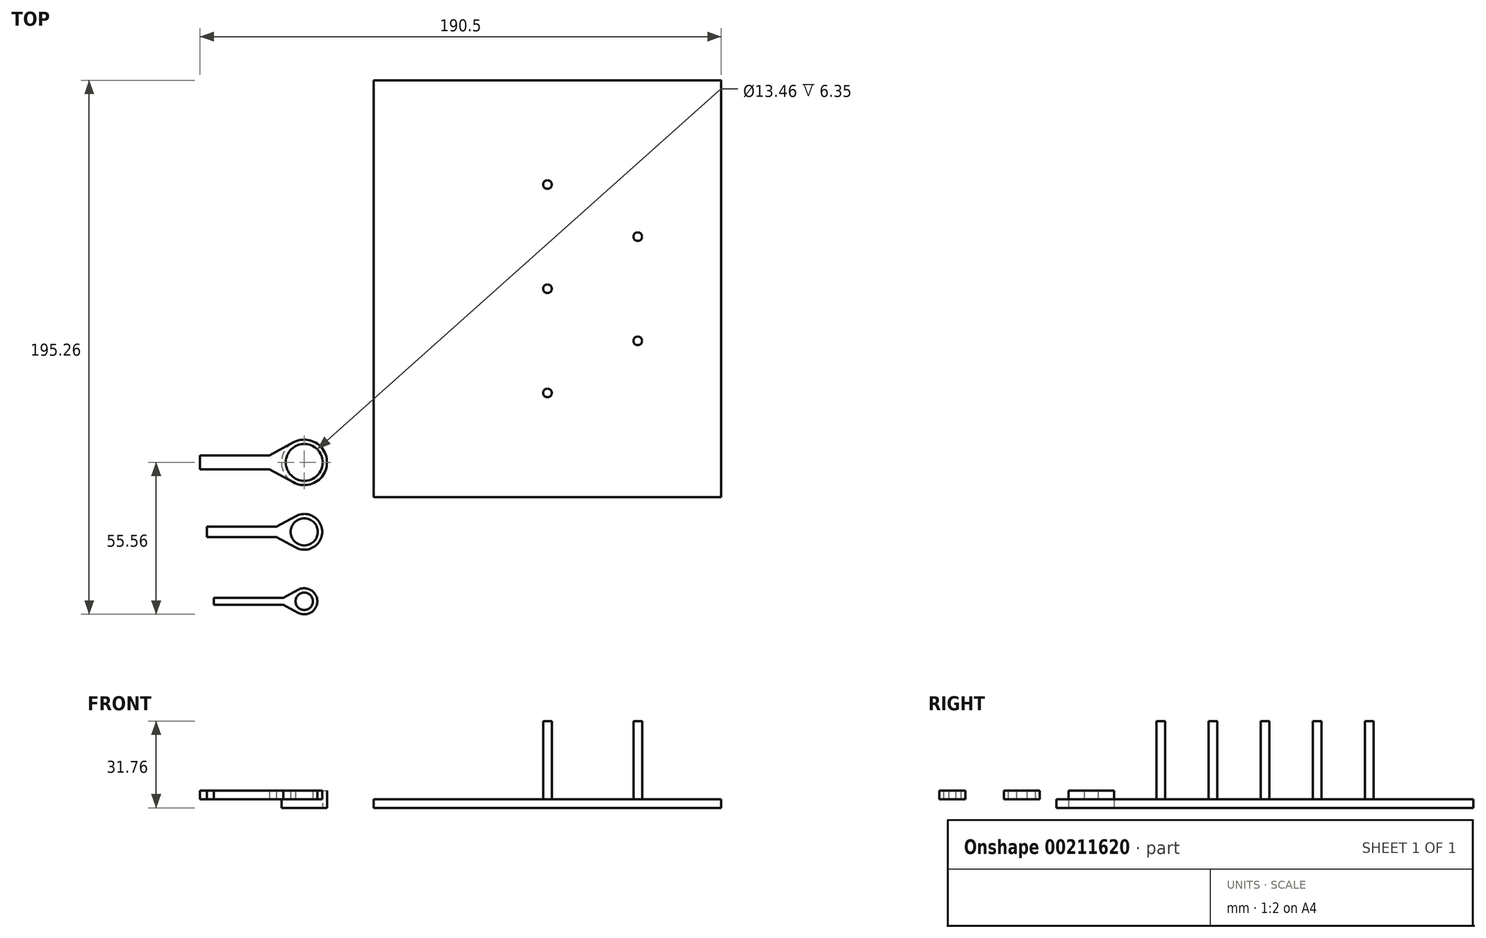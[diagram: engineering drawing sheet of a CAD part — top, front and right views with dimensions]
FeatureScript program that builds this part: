
annotation { "Feature Type Name" : "Feature", "Feature Type Description" : "" }
export const myFeature = defineFeature(function(context is Context, id is Id, definition is map)
    precondition{}
    {
        {
            var Q0;
            Q0=qCreatedBy(makeId("Top.planeOp"),FACE);
            var sketch = newSketch(context, id + "F0", { "sketchPlane" : qUnion([Q0])});
            skLineSegment(sketch, "E0.bottom", {"start": v(0, 152.4) * mm, "end": v(127, 152.4) * mm});
            skLineSegment(sketch, "E0.top", {"start": v(0, 0) * mm, "end": v(127, 0) * mm});
            skLineSegment(sketch, "E0.left", {"start": v(0, 152.4) * mm, "end": v(0, 0) * mm});
            skLineSegment(sketch, "E0.right", {"start": v(127, 152.4) * mm, "end": v(127, 0) * mm});
            skCircle(sketch, "E1", {"center": v(63.5, 76.2) * mm, "radius": 1.59 * mm});
            skCircle(sketch, "E2", {"center": v(63.5, 38.1) * mm, "radius": 1.59 * mm});
            skCircle(sketch, "E3.1.0", {"center": v(96.5, 57.15) * mm, "radius": 1.59 * mm});
            skCircle(sketch, "E3.2.0", {"center": v(96.5, 95.25) * mm, "radius": 1.59 * mm});
            skCircle(sketch, "E3.3.0", {"center": v(63.5, 114.3) * mm, "radius": 1.59 * mm});
            skCircle(sketch, "E3.4.0", {"center": v(30.5, 95.25) * mm, "radius": 1.59 * mm});
            skCircle(sketch, "E3.5.0", {"center": v(30.5, 57.15) * mm, "radius": 1.59 * mm});
            skCircle(sketch, "E4", {"center": v(-25.4, 12.7) * mm, "radius": 8.32 * mm});
            skLineSegment(sketch, "E5.bottom", {"start": v(-63.5, 15.24) * mm, "end": v(-38.1, 15.24) * mm});
            skLineSegment(sketch, "E5.top", {"start": v(-63.5, 10.16) * mm, "end": v(-38.1, 10.16) * mm});
            skLineSegment(sketch, "E5.left", {"start": v(-63.5, 15.24) * mm, "end": v(-63.5, 10.16) * mm});
            skLineSegment(sketch, "E5.right", {"start": v(-38.1, 15.24) * mm, "end": v(-38.1, 10.16) * mm});
            skLineSegment(sketch, "E6", {"start": v(-38.1, 15.24) * mm, "end": v(-29.39, 20) * mm});
            skLineSegment(sketch, "E7", {"start": v(-38.1, 10.16) * mm, "end": v(-29.39, 5.4) * mm});
            skLineSegment(sketch, "E8", {"start": v(-25.4, 12.7) * mm, "end": v(-38.1, 12.7) * mm});
            skCircle(sketch, "E9", {"center": v(-25.4, 12.7) * mm, "radius": 6.73 * mm});
            skCircle(sketch, "E10", {"center": v(-25.4, -12.7) * mm, "radius": 6.54 * mm});
            skLineSegment(sketch, "E11.bottom", {"start": v(-60.96, -10.8) * mm, "end": v(-35.56, -10.8) * mm});
            skLineSegment(sketch, "E11.top", {"start": v(-60.96, -14.6) * mm, "end": v(-35.56, -14.6) * mm});
            skLineSegment(sketch, "E11.left", {"start": v(-60.96, -10.8) * mm, "end": v(-60.96, -14.6) * mm});
            skLineSegment(sketch, "E11.right", {"start": v(-35.56, -10.8) * mm, "end": v(-35.56, -14.6) * mm});
            skLineSegment(sketch, "E12", {"start": v(-35.56, -10.8) * mm, "end": v(-28.53, -6.96) * mm});
            skLineSegment(sketch, "E13", {"start": v(-35.56, -14.6) * mm, "end": v(-28.53, -18.44) * mm});
            skLineSegment(sketch, "E14", {"start": v(-25.4, -12.7) * mm, "end": v(-35.56, -12.7) * mm});
            skCircle(sketch, "E15", {"center": v(-25.4, -12.7) * mm, "radius": 4.95 * mm});
            skCircle(sketch, "E16", {"center": v(-25.4, -38.1) * mm, "radius": 4.76 * mm});
            skLineSegment(sketch, "E17.bottom", {"start": v(-58.42, -36.83) * mm, "end": v(-33.02, -36.83) * mm});
            skLineSegment(sketch, "E17.top", {"start": v(-58.42, -39.37) * mm, "end": v(-33.02, -39.37) * mm});
            skLineSegment(sketch, "E17.left", {"start": v(-58.42, -36.83) * mm, "end": v(-58.42, -39.37) * mm});
            skLineSegment(sketch, "E17.right", {"start": v(-33.02, -36.83) * mm, "end": v(-33.02, -39.37) * mm});
            skLineSegment(sketch, "E18", {"start": v(-33.02, -36.83) * mm, "end": v(-27.68, -33.92) * mm});
            skLineSegment(sketch, "E19", {"start": v(-33.02, -39.37) * mm, "end": v(-27.68, -42.28) * mm});
            skLineSegment(sketch, "E20", {"start": v(-25.4, -38.1) * mm, "end": v(-33.02, -38.1) * mm});
            skCircle(sketch, "E21", {"center": v(-25.4, -38.1) * mm, "radius": 3.18 * mm});
            skSolve(sketch);
        }
        {
            var Q0;
            Q0=makeQuery(id+"F0.imprint","IMPRINT",FACE,{"disambiguationData":[TD([[makeQuery(id+"F0.imprint","IMPRINT",EDGE,{"derivedFrom":sQuery(id+"F0.wireOp",EDGE,"E0.bottom")}),-1.0]])]});
            var Q1;
            Q1=makeQuery(id+"F0.imprint","IMPRINT",FACE,{"disambiguationData":[TD([[makeQuery(id+"F0.imprint","IMPRINT",EDGE,{"derivedFrom":sQuery(id+"F0.wireOp",EDGE,"E3.3.0")}),1.0]])]});
            var Q2;
            Q2=makeQuery(id+"F0.imprint","IMPRINT",FACE,{"disambiguationData":[TD([[makeQuery(id+"F0.imprint","IMPRINT",EDGE,{"derivedFrom":sQuery(id+"F0.wireOp",EDGE,"E3.2.0")}),1.0]])]});
            var Q3;
            Q3=makeQuery(id+"F0.imprint","IMPRINT",FACE,{"disambiguationData":[TD([[makeQuery(id+"F0.imprint","IMPRINT",EDGE,{"derivedFrom":sQuery(id+"F0.wireOp",EDGE,"E3.1.0")}),1.0]])]});
            var Q4;
            Q4=makeQuery(id+"F0.imprint","IMPRINT",FACE,{"disambiguationData":[TD([[makeQuery(id+"F0.imprint","IMPRINT",EDGE,{"derivedFrom":sQuery(id+"F0.wireOp",EDGE,"E2")}),1.0]])]});
            var Q5;
            Q5=makeQuery(id+"F0.imprint","IMPRINT",FACE,{"disambiguationData":[TD([[makeQuery(id+"F0.imprint","IMPRINT",EDGE,{"derivedFrom":sQuery(id+"F0.wireOp",EDGE,"E3.5.0")}),1.0]])]});
            var Q6;
            Q6=makeQuery(id+"F0.imprint","IMPRINT",FACE,{"disambiguationData":[TD([[makeQuery(id+"F0.imprint","IMPRINT",EDGE,{"derivedFrom":sQuery(id+"F0.wireOp",EDGE,"E3.4.0")}),1.0]])]});
            var Q7;
            Q7=makeQuery(id+"F0.imprint","IMPRINT",FACE,{"disambiguationData":[TD([[makeQuery(id+"F0.imprint","IMPRINT",EDGE,{"derivedFrom":sQuery(id+"F0.wireOp",EDGE,"E1")}),1.0]])]});
            extrude(context, id + "F1", {"entities" : qUnion([Q0, Q1, Q2, Q3, Q4, Q5, Q6, Q7]), "oppositeDirection" : true, "depth" : 3.17 * mm});
        }
        {
            var Q0;
            Q0=makeQuery(id+"F0.imprint","IMPRINT",FACE,{"disambiguationData":[TD([[makeQuery(id+"F0.imprint","IMPRINT",EDGE,{"derivedFrom":sQuery(id+"F0.wireOp",EDGE,"E3.3.0")}),1.0]])]});
            var Q1;
            Q1=makeQuery(id+"F0.imprint","IMPRINT",FACE,{"disambiguationData":[TD([[makeQuery(id+"F0.imprint","IMPRINT",EDGE,{"derivedFrom":sQuery(id+"F0.wireOp",EDGE,"E3.2.0")}),1.0]])]});
            var Q2;
            Q2=makeQuery(id+"F0.imprint","IMPRINT",FACE,{"disambiguationData":[TD([[makeQuery(id+"F0.imprint","IMPRINT",EDGE,{"derivedFrom":sQuery(id+"F0.wireOp",EDGE,"E1")}),1.0]])]});
            var Q3;
            Q3=makeQuery(id+"F0.imprint","IMPRINT",FACE,{"disambiguationData":[TD([[makeQuery(id+"F0.imprint","IMPRINT",EDGE,{"derivedFrom":sQuery(id+"F0.wireOp",EDGE,"E3.1.0")}),1.0]])]});
            var Q4;
            Q4=makeQuery(id+"F0.imprint","IMPRINT",FACE,{"disambiguationData":[TD([[makeQuery(id+"F0.imprint","IMPRINT",EDGE,{"derivedFrom":sQuery(id+"F0.wireOp",EDGE,"E2")}),1.0]])]});
            var Q5;
            Q5=sQuery(id+"F0.wireOp",EDGE,"E3.3.0");
            var Q6;
            Q6=sQuery(id+"F0.wireOp",EDGE,"E3.2.0");
            var Q7;
            Q7=sQuery(id+"F0.wireOp",EDGE,"E3.1.0");
            var Q8;
            Q8=sQuery(id+"F0.wireOp",EDGE,"E2");
            var Q9;
            Q9=sQuery(id+"F0.wireOp",EDGE,"E3.5.0");
            var Q10;
            Q10=sQuery(id+"F0.wireOp",EDGE,"E3.4.0");
            var Q11;
            Q11=sQuery(id+"F0.wireOp",EDGE,"E1");
            extrude(context, id + "F2", {"entities" : qUnion([Q0, Q1, Q2, Q3, Q4]), "operationType" : NewBodyOperationType.ADD, "surfaceEntities" : qUnion([Q5, Q6, Q7, Q8, Q9, Q10, Q11]), "depth" : 28.57 * mm});
        }
        {
            var Q0;
            Q0=makeQuery(id+"F0.imprint","IMPRINT",FACE,{"disambiguationData":[TD([[makeQuery(id+"F0.imprint","IMPRINT",EDGE,{"derivedFrom":sQuery(id+"F0.wireOp",EDGE,"E9")}),-1.0]])]});
            var Q1;
            {var subQ0=sQuery(id+"F0.wireOp",EDGE,"E6");Q1=makeQuery(id+"F0.imprint","IMPRINT",FACE,{"disambiguationData":[TD([[makeQuery(id+"F0.imprint","IMPRINT",EDGE,{"derivedFrom":subQ0}),-1.0]])]});}
            var Q2;
            {var subQ0=sQuery(id+"F0.wireOp",EDGE,"E7");Q2=makeQuery(id+"F0.imprint","IMPRINT",FACE,{"disambiguationData":[TD([[makeQuery(id+"F0.imprint","IMPRINT",EDGE,{"derivedFrom":subQ0}),1.0]])]});}
            var Q3;
            {var subQ1=sQuery(id+"F0.wireOp",EDGE,"E5.bottom");Q3=makeQuery(id+"F0.imprint","IMPRINT",FACE,{"disambiguationData":[TD([[makeQuery(id+"F0.imprint","IMPRINT",EDGE,{"derivedFrom":subQ1}),-1.0]])]});}
            extrude(context, id + "F3", {"entities" : qUnion([Q0, Q1, Q2, Q3]), "depth" : 3.17 * mm});
        }
        {
            var Q0;
            Q0=makeQuery(id+"F0.imprint","IMPRINT",FACE,{"disambiguationData":[TD([[makeQuery(id+"F0.imprint","IMPRINT",EDGE,{"derivedFrom":sQuery(id+"F0.wireOp",EDGE,"E9")}),-1.0]])]});
            extrude(context, id + "F4", {"entities" : qUnion([Q0]), "operationType" : NewBodyOperationType.ADD, "oppositeDirection" : true, "depth" : 3.17 * mm});
        }
        {
            var Q0;
            Q0=makeQuery(id+"F0.imprint","IMPRINT",FACE,{"disambiguationData":[TD([[makeQuery(id+"F0.imprint","IMPRINT",EDGE,{"derivedFrom":sQuery(id+"F0.wireOp",EDGE,"E15")}),-1.0]])]});
            var Q1;
            {var subQ0=sQuery(id+"F0.wireOp",EDGE,"E13");Q1=makeQuery(id+"F0.imprint","IMPRINT",FACE,{"disambiguationData":[TD([[makeQuery(id+"F0.imprint","IMPRINT",EDGE,{"derivedFrom":subQ0}),1.0]])]});}
            var Q2;
            {var subQ0=sQuery(id+"F0.wireOp",EDGE,"E12");Q2=makeQuery(id+"F0.imprint","IMPRINT",FACE,{"disambiguationData":[TD([[makeQuery(id+"F0.imprint","IMPRINT",EDGE,{"derivedFrom":subQ0}),-1.0]])]});}
            var Q3;
            {var subQ1=sQuery(id+"F0.wireOp",EDGE,"E11.bottom");Q3=makeQuery(id+"F0.imprint","IMPRINT",FACE,{"disambiguationData":[TD([[makeQuery(id+"F0.imprint","IMPRINT",EDGE,{"derivedFrom":subQ1}),-1.0]])]});}
            extrude(context, id + "F5", {"entities" : qUnion([Q0, Q1, Q2, Q3]), "depth" : 3.17 * mm});
        }
        {
            var Q0;
            Q0=makeQuery(id+"F0.imprint","IMPRINT",FACE,{"disambiguationData":[TD([[makeQuery(id+"F0.imprint","IMPRINT",EDGE,{"derivedFrom":sQuery(id+"F0.wireOp",EDGE,"E21")}),-1.0]])]});
            var Q1;
            {var subQ0=sQuery(id+"F0.wireOp",EDGE,"E18");Q1=makeQuery(id+"F0.imprint","IMPRINT",FACE,{"disambiguationData":[TD([[makeQuery(id+"F0.imprint","IMPRINT",EDGE,{"derivedFrom":subQ0}),-1.0]])]});}
            var Q2;
            {var subQ0=sQuery(id+"F0.wireOp",EDGE,"E19");Q2=makeQuery(id+"F0.imprint","IMPRINT",FACE,{"disambiguationData":[TD([[makeQuery(id+"F0.imprint","IMPRINT",EDGE,{"derivedFrom":subQ0}),1.0]])]});}
            var Q3;
            {var subQ1=sQuery(id+"F0.wireOp",EDGE,"E17.bottom");Q3=makeQuery(id+"F0.imprint","IMPRINT",FACE,{"disambiguationData":[TD([[makeQuery(id+"F0.imprint","IMPRINT",EDGE,{"derivedFrom":subQ1}),-1.0]])]});}
            extrude(context, id + "F6", {"entities" : qUnion([Q0, Q1, Q2, Q3]), "depth" : 3.17 * mm});
        }
    });
